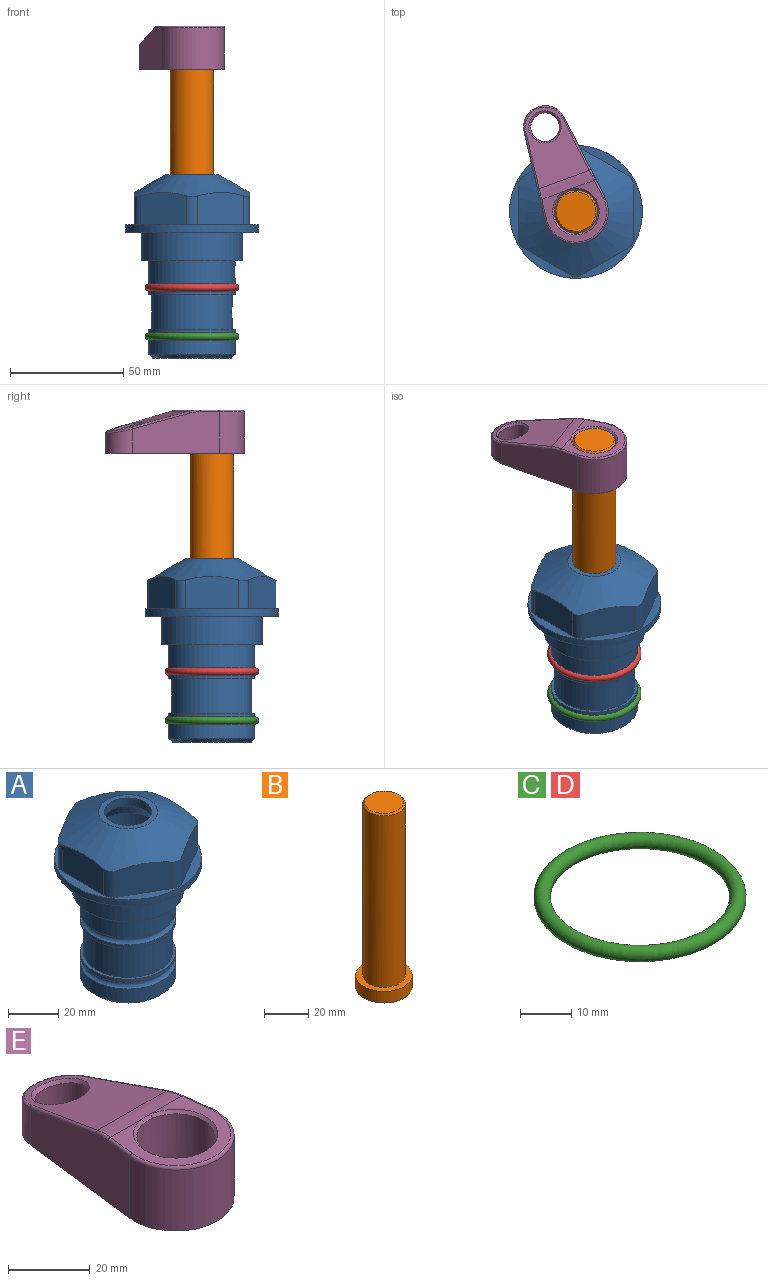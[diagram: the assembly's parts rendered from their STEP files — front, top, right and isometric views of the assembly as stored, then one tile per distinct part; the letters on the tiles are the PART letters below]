
ASSEMBLY  parts=5 mates=4
PART A: 36 faces, bbox 58.7x58.7x81 mm
  f0: cylinder r=17.78mm len=35.56mm, axis (0,0,1), area 1670.8mm2, adj f23,f24,f31
  f1: cylinder r=19.05mm len=38.1mm, axis (0,0,1), area 1191.9mm2, adj f26,f27,f30
  f2: plane 58.66x58.66mm, normal (0,0,-1), area 1150.6mm2, adj f3,f28
  f3: cylinder r=29.33mm len=58.66mm, axis (0,0,-1), area 585.1mm2, adj f2,f4
  f4: plane 58.66x58.66mm, normal (0,0,1), area 475.9mm2, adj f3,f5,f6,f7,f8,f9,f10,f11
  f5: plane 20.32x14.34mm, normal (-0.5,0.87,0), area 324.4mm2, adj f4,f15,f16,f17
  f6: plane 20.32x14.34mm, normal (0.5,0.87,0), area 324.4mm2, adj f4,f14,f15,f17
  f7: plane 23.48x14.34mm, normal (1,0,0), area 324.4mm2, adj f4,f13,f14,f17
  f8: plane 20.32x14.34mm, normal (0.5,-0.87,0), area 324.4mm2, adj f4,f12,f13,f17
  f9: plane 20.32x14.34mm, normal (-0.5,-0.87,0), area 324.4mm2, adj f4,f11,f12,f17
  f10: plane 23.48x14.34mm, normal (-1,0,0), area 324.4mm2, adj f4,f11,f16,f17
  f11: cylinder r=5.08mm len=12.85mm, axis (0,0,-1), area 67.2mm2, adj f4,f9,f10,f17
  f12: cylinder r=5.08mm len=12.85mm, axis (0,0,-1), area 67.2mm2, adj f4,f8,f9,f17
  f13: cylinder r=5.08mm len=12.85mm, axis (0,0,-1), area 67.2mm2, adj f4,f7,f8,f17
  f14: cylinder r=5.08mm len=12.85mm, axis (0,0,-1), area 67.2mm2, adj f4,f6,f7,f17
  f15: cylinder r=5.08mm len=12.85mm, axis (0,0,-1), area 67.2mm2, adj f4,f5,f6,f17
  f16: cylinder r=5.08mm len=12.85mm, axis (0,0,-1), area 67.2mm2, adj f4,f5,f10,f17
  f17: cone r=11.73mm half-angle=60deg, axis (0,0,-1), area 2071.8mm2, adj f5,f6,f7,f8,f9,f10,f11,f12
  f18: plane 23.46x23.46mm, normal (0,0,1), area 147.4mm2, adj f17,f35
  f19: plane 34.93x34.93mm, normal (0,0,-1), area 958mm2, adj f29
  f20: cylinder r=19.05mm len=38.1mm, axis (0,0,1), area 760.1mm2, adj f21,f29
  f21: torus R=19.05mm, axis (0,0,1), area 565.3mm2, adj f20,f22
  f22: cylinder r=19.05mm len=38.1mm, axis (0,0,1), area 190mm2, adj f21,f23
  f23: plane 38.1x38.1mm, normal (0,0,1), area 146.9mm2, adj f0,f22
  f24: plane 38.1x38.1mm, normal (0,0,-1), area 146.9mm2, adj f0,f25
  f25: cylinder r=19.05mm len=38.1mm, axis (0,0,1), area 190mm2, adj f24,f26
  f26: torus R=19.05mm, axis (0,0,1), area 565.3mm2, adj f1,f25
  f27: plane 44.45x44.45mm, normal (0,0,-1), area 411.7mm2, adj f1,f28
  f28: cylinder r=22.23mm len=44.45mm, axis (0,0,1), area 1773.5mm2, adj f2,f27
  f29: cone r=19.05mm half-angle=45deg, axis (0,0,1), area 257.5mm2, adj f19,f20
  f30: cylinder r=3.17mm len=6.75mm, axis (-1,0,0), area 128mm2, adj f1,f33
  f31: cylinder r=3.17mm len=6.35mm, axis (-1,0,0), area 102.5mm2, adj f0,f33
  f32: plane 25.4x25.4mm, normal (0,0,1), area 506.7mm2, adj f33
  f33: cylinder r=12.7mm len=66.42mm, axis (0,0,-1), area 5236.2mm2, adj f30,f31,f32,f34
  f34: cone r=9.53mm half-angle=30deg, axis (0,0,-1), area 443.4mm2, adj f33,f35
  f35: cylinder r=9.53mm len=19.05mm, axis (0,0,-1), area 240.9mm2, adj f18,f34
PART B: 6 faces, bbox 25.4x25.4x101.6 mm
  f0: plane 17.46x17.46mm, normal (0,0,1), area 239.5mm2, adj f5
  f1: plane 25.4x25.4mm, normal (0,0,-1), area 506.7mm2, adj f2
  f2: cylinder r=12.7mm len=25.4mm, axis (0,0,1), area 506.7mm2, adj f1,f3
  f3: plane 25.4x25.4mm, normal (0,0,1), area 221.7mm2, adj f2,f4
  f4: cylinder r=9.53mm len=94.46mm, axis (0,0,1), area 5653mm2, adj f3,f5
  f5: cone r=8.73mm half-angle=45deg, axis (0,0,-1), area 64.4mm2, adj f0,f4
PART C: 1 faces, bbox 44.7x44.7x3.2 mm
  f0: torus R=19.05mm, axis (0,0,1), area 1193.9mm2
PART D: same geometry as C
PART E: 31 faces, bbox 31.7x65.5x19.8 mm
  f0: plane 39.12x18.26mm, normal (0.99,0.12,0), area 612.2mm2, adj f1,f4,f7,f11,f13,f15
  f1: cylinder r=9.53mm len=18.91mm, axis (0,0,-1), area 296.1mm2, adj f0,f2,f7,f17
  f2: plane 39.12x18.26mm, normal (-0.99,0.12,0), area 612.2mm2, adj f1,f4,f7,f12,f14,f16
  f3: cylinder r=6.35mm len=12.7mm, axis (0,0,-1), area 362.4mm2, adj f7,f18
  f4: cylinder r=14.29mm len=28.58mm, axis (0,0,-1), area 882.2mm2, adj f0,f2,f7,f10
  f5: cylinder r=9.53mm len=19.05mm, axis (0,0,-1), area 1092.6mm2, adj f7,f19,f20
  f6: plane 26.99x23.69mm, normal (0,0,1), area 216.2mm2, adj f9,f10,f11,f12,f19
  f7: plane 63.5x28.58mm, normal (0,0,-1), area 661.8mm2, adj f0,f1,f2,f3,f4,f5,f22,f23
  f8: plane 33.52x23.6mm, normal (0,0.26,0.97), area 486mm2, adj f9,f15,f16,f17,f18
  f9: cylinder r=19.05mm len=24.72mm, axis (1,0,0), area 120.4mm2, adj f6,f8,f13,f14,f20
  f10: torus R=13.49mm, axis (0,0,1), area 59mm2, adj f4,f6,f11,f12
  f11: cylinder r=0.79mm len=8.67mm, axis (0.12,-0.99,0), area 10.8mm2, adj f0,f6,f10,f13
  f12: cylinder r=0.79mm len=8.67mm, axis (0.12,0.99,0), area 10.8mm2, adj f2,f6,f10,f14
  f13: bspline ~4.95x1.42mm, area 6.1mm2, adj f0,f9,f11,f15
  f14: bspline ~4.95x1.42mm, area 6.1mm2, adj f2,f9,f12,f16
  f15: cylinder r=0.79mm len=25.95mm, axis (0.12,-0.96,0.26), area 32.9mm2, adj f0,f8,f13,f17
  f16: cylinder r=0.79mm len=25.95mm, axis (0.12,0.96,-0.26), area 32.9mm2, adj f2,f8,f14,f17
  f17: bspline ~18.91x8.38mm, area 30mm2, adj f1,f8,f15,f16
  f18: bspline ~14.29x14.29mm, area 48.3mm2, adj f3,f8
  f19: cone r=9.53mm half-angle=45deg, axis (0,0,1), area 66.5mm2, adj f5,f6,f20
  f20: bspline ~3.22x0.96mm, area 3.5mm2, adj f5,f9,f19
  f21: plane 2.75x2.72mm, normal (0,0,-1), area 2.9mm2, adj f23,f25,f28
  f22: plane 23.05x15.88mm, normal (-0.99,-0.12,0), area 323.6mm2, adj f7,f25,f26,f27,f28,f29
  f23: plane 23.05x15.88mm, normal (0.99,-0.12,0), area 323.6mm2, adj f7,f21,f25,f27,f28,f30
  f24: cylinder r=9.53mm len=10.69mm, axis (0,0,-1), area 114.7mm2, adj f7,f27,f29,f30
  f25: cylinder r=12.7mm len=20.59mm, axis (0,0,-1), area 381.1mm2, adj f7,f21,f22,f23,f26,f28
  f26: plane 2.75x2.72mm, normal (0,0,-1), area 2.9mm2, adj f22,f25,f28
  f27: plane 19.72x18.37mm, normal (0,-0.26,-0.97), area 291.8mm2, adj f22,f23,f24,f28,f29,f30
  f28: cylinder r=15.88mm len=19.92mm, axis (1,0,0), area 54.8mm2, adj f21,f22,f23,f25,f26,f27
  f29: cylinder r=1.59mm len=11mm, axis (0,0,-1), area 34.7mm2, adj f7,f22,f24,f27
  f30: cylinder r=1.59mm len=11mm, axis (0,0,-1), area 34.7mm2, adj f7,f23,f24,f27
PLACE A at identity fixed
PLACE B rot(axis=(0,0,1),20.1deg) t=(0,0,27.55)mm
PLACE C t=(0,0,-21.59)mm
PLACE D at identity
PLACE E rot(axis=(0,0,1),20.1deg) t=(0,0,27.55)mm
MATE fastened C.f0 <-> A.f0  axis (0,0,1) through (0,0,-46.1)mm
MATE fastened D.f0 <-> A.f0  axis (0,0,1) through (0,0,-24.51)mm
MATE fastened B.f2 <-> E.f4  axis (0,0,1) through (0,0,91.05)mm
MATE cylindrical A.f0 <-> B.f2  axis (0,0,1) through (0,0,-50.55)mm
